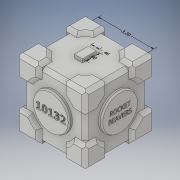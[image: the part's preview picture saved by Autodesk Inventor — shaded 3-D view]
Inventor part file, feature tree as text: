
AUTODESK INVENTOR PART (.ipt)
format: ipt  version: 2018 (Build 220112000, 112)  size: 1,693,184 bytes
history: native  units: in
note: dims shown in document units (in); Inventor stores cm internally (conversion verified against a paired STEP export)
features: chamfer x106, sketch x23, extrude x19, fillet x9, other x4, emboss x4
ambient origin geometry x8: Origin, YZ Plane, XZ Plane, XY Plane, X Axis, Y Axis, Z Axis, Center Point
bodies: Solid1 (feature_tree)
feature tree (165):
  other  "Annotations"
  extrude  "Extrusion1"  Depth=4.0in
  extrude  "Extrusion2"  Depth=1.3in
  extrude  "Extrusion3"  Depth=1.3in
  extrude  "Extrusion4"  Depth=1.3in
  extrude  "Extrusion5"  Depth=1.3in
  extrude  "Extrusion6"  Depth=0.2in
  chamfer  "Chamfer42"  Distance=0.2in
  chamfer  "Chamfer43"  Distance=0.2in
  chamfer  "Chamfer44"  Distance=0.2in
  chamfer  "Chamfer45"  Distance=0.2in
  chamfer  "Chamfer46"  Distance=0.2in Angle=45.0deg
  chamfer  "Chamfer47"  Distance=0.2in Angle=45.0deg
  chamfer  "Chamfer48"  Distance=0.2in Angle=45.0deg
  chamfer  "Chamfer49"  Distance=0.2in Angle=45.0deg
  chamfer  "Chamfer50"  Distance=0.2in Angle=45.0deg
  chamfer  "Chamfer51"  Distance=0.2in Angle=45.0deg
  chamfer  "Chamfer52"  Distance=0.2in Angle=45.0deg
  chamfer  "Chamfer53"  Distance=0.2in Angle=45.0deg
  chamfer  "Chamfer54"  Distance=0.2in Angle=45.0deg
  chamfer  "Chamfer55"  Distance=0.2in Angle=45.0deg
  chamfer  "Chamfer56"  Distance=0.2in Angle=45.0deg
  chamfer  "Chamfer57"  Distance=0.2in Angle=45.0deg
  chamfer  "Chamfer58"  Distance=0.2in Angle=45.0deg
  chamfer  "Chamfer59"  Distance=0.2in Angle=45.0deg
  chamfer  "Chamfer60"  Distance=0.2in Angle=45.0deg
  chamfer  "Chamfer61"  Distance=0.2in Angle=45.0deg
  chamfer  "Chamfer62"  Distance=0.2in Angle=45.0deg
  chamfer  "Chamfer63"  Distance=0.2in Angle=45.0deg
  chamfer  "Chamfer64"  Distance=0.2in Angle=45.0deg
  chamfer  "Chamfer65"  Distance=0.2in Angle=45.0deg
  chamfer  "Chamfer66"  Distance=0.2in Angle=45.0deg
  chamfer  "Chamfer67"  Distance=0.2in Angle=45.0deg
  chamfer  "Chamfer68"  Distance=0.2in Angle=45.0deg
  chamfer  "Chamfer69"  Distance=0.2in Angle=45.0deg
  chamfer  "Chamfer70"  Distance=0.2in Angle=45.0deg
  chamfer  "Chamfer71"  Distance=0.2in Angle=45.0deg
  chamfer  "Chamfer72"  Distance=0.2in Angle=45.0deg
  chamfer  "Chamfer73"  Distance=0.2in Angle=45.0deg
  chamfer  "Chamfer74"  Distance=0.2in Angle=45.0deg
  chamfer  "Chamfer75"  Distance=0.2in Angle=45.0deg
  chamfer  "Chamfer76"  Distance=0.2in Angle=45.0deg
  chamfer  "Chamfer77"  Distance=0.2in Angle=45.0deg
  chamfer  "Chamfer78"  Distance=0.2in Angle=45.0deg
  chamfer  "Chamfer79"  Distance=0.2in Angle=45.0deg
  chamfer  "Chamfer80"  Distance=0.2in Angle=45.0deg
  chamfer  "Chamfer81"  Distance=0.2in Angle=45.0deg
  chamfer  "Chamfer82"  Distance=0.2in Angle=45.0deg
  chamfer  "Chamfer83"  Distance=0.2in Angle=45.0deg
  chamfer  "Chamfer84"  Distance=0.2in Angle=45.0deg
  chamfer  "Chamfer85"  Distance=0.2in Angle=45.0deg
  chamfer  "Chamfer86"  Distance=0.2in Angle=45.0deg
  chamfer  "Chamfer87"  Distance=0.2in Angle=45.0deg
  chamfer  "Chamfer88"  Distance=0.2in Angle=45.0deg
  chamfer  "Chamfer89"  Distance=0.2in Angle=45.0deg
  chamfer  "Chamfer90"  Distance=0.2in Angle=45.0deg
  chamfer  "Chamfer91"  Distance=0.2in Angle=45.0deg
  chamfer  "Chamfer92"  Distance=0.2in Angle=45.0deg
  chamfer  "Chamfer93"  Distance=0.2in Angle=45.0deg
  chamfer  "Chamfer94"  Distance=0.2in Angle=45.0deg
  chamfer  "Chamfer95"  Distance=0.2in Angle=45.0deg
  chamfer  "Chamfer96"  Distance=0.2in Angle=45.0deg
  chamfer  "Chamfer97"  Distance=0.2in Angle=45.0deg
  chamfer  "Chamfer98"  Distance=0.2in Angle=45.0deg
  chamfer  "Chamfer99"  Distance=0.2in Angle=45.0deg
  chamfer  "Chamfer100"  Distance=0.2in Angle=45.0deg
  chamfer  "Chamfer101"  Distance=0.2in Angle=45.0deg
  chamfer  "Chamfer102"  Distance=0.2in Angle=45.0deg
  chamfer  "Chamfer103"  Distance=0.2in Angle=45.0deg
  chamfer  "Chamfer104"  Distance=0.2in Angle=45.0deg
  chamfer  "Chamfer105"  Distance=0.2in Angle=45.0deg
  chamfer  "Chamfer106"  Distance=0.2in Angle=45.0deg
  chamfer  "Chamfer107"  Distance=0.2in Angle=45.0deg
  chamfer  "Chamfer108"  Distance=0.2in Angle=45.0deg
  chamfer  "Chamfer109"  Distance=0.2in Angle=45.0deg
  chamfer  "Chamfer110"  Distance=0.2in Angle=45.0deg
  chamfer  "Chamfer111"  Distance=0.2in Angle=45.0deg
  chamfer  "Chamfer112"  Distance=0.2in Angle=45.0deg
  chamfer  "Chamfer113"  Distance=0.2in Angle=45.0deg
  chamfer  "Chamfer114"  Distance=0.2in Angle=45.0deg
  chamfer  "Chamfer115"  Distance=0.2in Angle=45.0deg
  chamfer  "Chamfer116"  Distance=0.2in Angle=45.0deg
  chamfer  "Chamfer117"  Distance=0.2in Angle=45.0deg
  extrude  "Extrusion7"  Depth=0.2in TaperAngle=45.0deg
  extrude  "Extrusion8"  Depth=0.2in TaperAngle=45.0deg
  extrude  "Extrusion9"  Depth=0.2in TaperAngle=0.0deg
  extrude  "Extrusion10"  Depth=0.2in TaperAngle=0.0deg
  chamfer  "Chamfer118"  Distance=0.2in
  chamfer  "Chamfer119"  Distance=0.2in
  chamfer  "Chamfer120"  Distance=0.2in Angle=45.0deg
  chamfer  "Chamfer121"  Distance=0.2in Angle=45.0deg
  chamfer  "Chamfer122"  Distance=0.2in Angle=45.0deg
  chamfer  "Chamfer123"  Distance=0.2in Angle=45.0deg
  chamfer  "Chamfer124"  Distance=0.2in Angle=45.0deg
  chamfer  "Chamfer125"  Distance=0.2in Angle=45.0deg
  chamfer  "Chamfer126"  Distance=0.2in Angle=45.0deg
  chamfer  "Chamfer127"  Distance=0.2in Angle=45.0deg
  chamfer  "Chamfer128"  Distance=0.2in Angle=45.0deg
  chamfer  "Chamfer129"  Distance=0.2in Angle=45.0deg
  chamfer  "Chamfer130"  Distance=0.2in Angle=45.0deg
  chamfer  "Chamfer131"  Distance=0.2in Angle=45.0deg
  chamfer  "Chamfer132"  Distance=0.2in Angle=45.0deg
  chamfer  "Chamfer133"  Distance=0.2in Angle=45.0deg
  extrude  "Extrusion11"  Depth=0.2in TaperAngle=45.0deg
  chamfer  "Chamfer134"  Distance=0.2in
  chamfer  "Chamfer135"  Distance=0.2in Angle=45.0deg
  chamfer  "Chamfer136"  Distance=0.2in Angle=45.0deg
  chamfer  "Chamfer137"  Distance=0.2in Angle=45.0deg
  extrude  "Extrusion12"  Depth=0.2in
  sketch  "Sketch16"  dims[d379=2.8in d380=0.2in d381=0.0in]
  sketch  "Sketch17"  dims[d382=2.8in d383=0.2in d384=0.0in]
  extrude  "Extrusion13"  Depth=0.2in
  extrude  "Extrusion14"  Depth=2.1in
  extrude  "Extrusion15"  Depth=0.2in TaperAngle=0.0deg
  chamfer  "Chamfer138"  Distance=0.2in
  chamfer  "Chamfer139"  Distance=0.1in Angle=45.0deg
  chamfer  "Chamfer140"  Distance=0.1in Angle=45.0deg
  chamfer  "Chamfer141"  Distance=0.1in Angle=45.0deg
  extrude  "Extrusion16"  Depth=0.2in
  extrude  "Extrusion17"  Depth=0.46in TaperAngle=0.0deg
  chamfer  "Chamfer142"  Distance=1.8in
  chamfer  "Chamfer143"  Distance=1.0in
  fillet  "Fillet1"  Radius=0.8in
  fillet  "Fillet2"  Radius=0.8in
  fillet  "Fillet3"  Radius=1.1in
  fillet  "Fillet4"  Radius=1.1in
  fillet  "Fillet5"  Radius=0.1in
  fillet  "Fillet6"  Radius=0.1in
  fillet  "Fillet7"  Radius=0.1in
  fillet  "Fillet8"  Radius=0.1in
  emboss  "Emboss1"
  emboss  "Emboss2"
  emboss  "Emboss3"
  emboss  "Emboss4"
  extrude  "Extrusion18"  Depth=0.1in
  chamfer  "Chamfer144"  Distance=0.1in
  chamfer  "Chamfer145"  Distance=0.2in
  chamfer  "Chamfer146"  Distance=0.2in
  chamfer  "Chamfer147"  Distance=0.2in
  fillet  "Fillet9"  Radius=0.2in
  extrude  "Extrusion19"  Depth=0.46in
  sketch  "Sketch1"  dims[d0=4.0in d1=4.0in]
  sketch  "Sketch2"  dims[d2=4.0in d3=0.0in d4=1.3in]
  sketch  "Sketch3"  dims[d5=1.3in d6=1.3in]
  sketch  "Sketch4"  dims[d7=1.3in d8=1.3in]
  sketch  "Sketch5"  dims[d9=1.3in d10=1.3in]
  sketch  "Sketch6"  dims[d11=0.2in d12=0.0in d13=1.3in]
  sketch  "Sketch9"  dims[d14=1.3in]
  sketch  "Sketch11"  dims[d15=1.3in]
  sketch  "Sketch12"  dims[d16=1.3in d17=0.2in d18=0.0in d19=0.2in d20=0.0in d21=0.2in d22=0.0in d23=0.2in d24=0.0in d148=0.2in d149=0.2in d150=45.0deg d151=0.2in d152=0.2in d153=45.0deg d154=0.2in d155=0.2in d156=45.0deg d157=0.2in d158=0.2in d159=45.0deg d160=0.2in d161=0.2in d162=45.0deg d163=0.2in d164=0.2in d165=45.0deg d166=0.2in d167=0.2in d168=45.0deg d169=0.2in d170=0.2in d171=45.0deg d172=0.2in d173=0.2in d174=45.0deg d175=0.2in d176=0.2in d177=45.0deg d178=0.2in d179=0.2in d180=45.0deg d181=0.2in d182=0.2in d183=45.0deg d184=0.2in d185=0.2in d186=45.0deg d187=0.2in d188=0.2in d189=45.0deg d190=0.2in d191=0.2in d192=45.0deg d193=0.2in d194=0.2in d195=45.0deg d196=0.2in d197=0.2in d198=45.0deg d199=0.2in d200=0.2in d201=45.0deg d202=0.2in d203=0.2in d204=45.0deg d205=0.2in d206=0.2in d207=45.0deg d208=0.2in d209=0.2in d210=45.0deg d211=0.2in d212=0.2in d213=45.0deg d214=0.2in d215=0.2in d216=45.0deg d217=0.2in d218=0.2in d219=45.0deg d220=0.2in d221=0.2in d222=45.0deg d223=0.2in d224=0.2in d225=45.0deg d226=0.2in d227=0.2in d228=45.0deg d229=0.2in d230=0.2in d231=45.0deg d232=0.2in d233=0.2in d234=45.0deg d235=0.2in d236=0.2in d237=45.0deg d238=0.2in d239=0.2in d240=45.0deg d241=0.2in d242=0.2in d243=45.0deg d244=0.2in d245=0.2in d246=45.0deg d247=0.2in d248=0.2in d249=45.0deg d250=0.2in d251=0.2in d252=45.0deg d253=0.2in d254=0.2in d255=45.0deg d256=0.2in d257=0.2in d258=45.0deg d259=0.2in d260=0.2in d261=45.0deg d262=0.2in d263=0.2in d264=45.0deg d265=0.2in d266=0.2in d267=45.0deg d268=0.2in d269=0.2in d270=45.0deg d271=0.2in d272=0.2in d273=45.0deg d274=0.2in d275=0.2in d276=45.0deg d277=0.2in d278=0.2in d279=45.0deg d280=0.2in d281=0.2in d282=45.0deg d283=0.2in d284=0.2in d285=45.0deg d286=0.2in d287=0.2in d288=45.0deg d289=0.2in d290=0.2in d291=45.0deg d292=0.2in d293=0.2in d294=45.0deg d295=0.2in d296=0.2in d297=45.0deg d298=0.2in d299=0.2in d300=45.0deg d301=0.2in d302=0.2in d303=45.0deg d304=0.2in d305=0.2in d306=45.0deg d307=0.2in d308=0.2in d309=45.0deg d310=0.2in d311=0.2in d312=45.0deg d313=0.2in d314=0.2in d315=45.0deg d316=0.2in d317=0.2in d318=45.0deg d319=0.2in d320=0.2in d321=45.0deg d322=0.2in d323=0.2in d324=45.0deg d325=0.2in d326=0.2in d327=45.0deg d328=0.2in d329=0.2in d330=45.0deg d331=0.2in d332=0.2in d333=45.0deg d334=0.2in d335=0.2in d336=45.0deg d337=0.2in d338=0.2in d339=45.0deg d340=0.2in d341=0.2in d342=45.0deg d343=0.2in d344=0.2in d345=45.0deg d346=0.2in d347=0.2in d348=45.0deg d349=0.2in d350=0.2in d351=45.0deg d352=0.2in d353=0.2in d354=45.0deg d355=0.2in d356=0.2in d357=45.0deg d358=0.2in d359=0.2in d360=45.0deg d361=0.2in d362=0.2in d363=45.0deg]
  sketch  "Sketch13"  dims[d364=0.2in d365=0.2in d366=45.0deg d367=0.2in d368=0.2in d369=45.0deg]
  sketch  "Sketch14"  dims[d370=0.2in d371=0.2in d372=45.0deg d373=0.2in d374=0.2in d375=45.0deg]
  sketch  "Sketch15"  dims[d376=2.8in d377=0.2in d378=0.0in]
  sketch  "Sketch18"  dims[d385=2.8in d386=0.2in d387=0.0in d388=0.2in d389=0.2in d390=45.0deg d391=0.2in d392=0.2in d393=45.0deg d394=0.2in d395=0.2in d396=45.0deg d397=0.2in d398=0.2in d399=45.0deg d400=0.2in d401=0.2in d402=45.0deg d403=0.2in d404=0.2in d405=45.0deg d406=0.2in d407=0.2in d408=45.0deg d409=0.2in d410=0.2in d411=45.0deg d412=0.2in d413=0.2in d414=45.0deg d415=0.2in d416=0.2in d417=45.0deg d418=0.2in d419=0.2in d420=45.0deg d421=0.2in d422=0.2in d423=45.0deg d424=0.2in d425=0.2in d426=45.0deg d427=0.2in d428=0.2in d429=45.0deg]
  sketch  "Sketch19"  dims[d430=0.2in d431=0.2in d432=45.0deg d433=0.2in d434=0.2in d435=45.0deg]
  sketch  "Sketch20"  dims[d436=2.8in d437=0.2in d438=0.0in d439=0.2in d440=0.2in d441=45.0deg d442=0.2in d443=0.2in d444=45.0deg d445=0.2in d446=0.2in d447=45.0deg]
  sketch  "Sketch21"  dims[d448=0.2in d449=0.2in d450=45.0deg d451=2.1in]
  sketch  "Sketch22"  dims[d452=0.2in d453=0.0in d454=2.1in]
  sketch  "Sketch23"  dims[d455=2.1in d456=2.1in]
  sketch  "Sketch24"  dims[d457=0.2in d458=0.0in d459=0.2in d460=0.0in d461=0.2in d462=0.0in d463=0.05in d464=0.1in d465=45.0deg d466=0.05in d467=0.1in d468=45.0deg d469=0.05in d470=0.1in d471=45.0deg]
  sketch  "Sketch25"  dims[d472=0.05in d473=0.1in d474=45.0deg d475=0.2in]
  sketch  "Sketch26"  dims[d476=0.2in d477=3.0in d478=0.0in d479=1.8in d480=1.0in d481=0.0in d488=0.8in d489=3.0in d490=45.0deg d491=0.8in d492=3.0in d493=45.0deg d494=1.1in d495=1.1in d496=0.1in d497=0.1in d498=0.1in d499=0.1in d500=0.1in d501=0.1in d502=0.2in d503=0.0in d504=0.2in d505=0.0in d506=0.2in d507=0.0in d508=0.2in d509=0.0in d513=0.7in d514=0.7in d515=0.7in d516=0.7in d517=1.2in d518=0.0in d519=1.2in d520=0.15in d521=45.0deg d522=1.2in d523=0.15in d524=45.0deg d525=1.2in d526=0.15in d527=45.0deg d528=1.2in d529=0.15in d530=45.0deg d531=0.1in d537=0.4in d538=0.23in d539=0.8in d540=0.46in d541=0.2in d542=0.0in d546=1.0in d547=3.2in d548=0.1438in d549=0.251in d550=0.8in d551=0.156in d552=0.2976in d553=0.46in d557=0.2824in d558=0.1827in d559=3.2in]
  other  "Linear Dimension 7"
  other  "Linear Dimension 8"
  other  "Linear Dimension 9"
